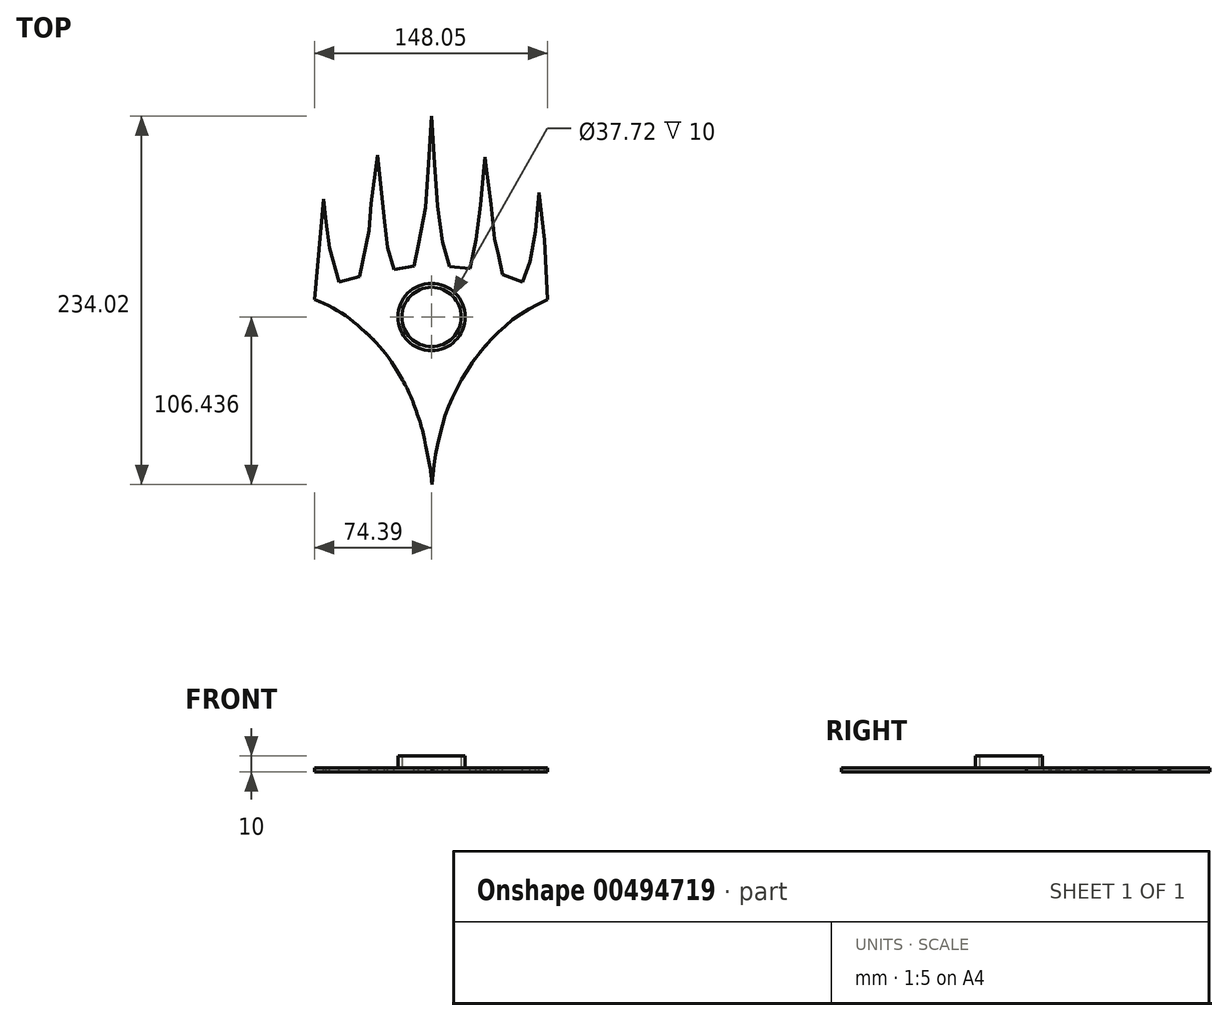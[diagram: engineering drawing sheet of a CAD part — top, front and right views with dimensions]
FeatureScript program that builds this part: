
annotation { "Feature Type Name" : "Feature", "Feature Type Description" : "" }
export const myFeature = defineFeature(function(context is Context, id is Id, definition is map)
    precondition{}
    {
        {
            var Q0;
            Q0=qCreatedBy(makeId("Top.planeOp"),FACE);
            var sketch = newSketch(context, id + "F0", { "sketchPlane" : qUnion([Q0])});
            skFitSpline(sketch, "E0", {"points": [v(-77.05, -65.7) * mm, v(-66.03, -70.4) * mm, v(-54.89, -77.21) * mm, v(-43.29, -86.88) * mm, v(-32.6, -98.12) * mm, v(-24.04, -110.73) * mm, v(-17.04, -122.98) * mm, v(-12.72, -133.75) * mm, v(-8.2, -147.47) * mm, v(-6, -157.78) * mm, v(-3.7, -169.2) * mm, v(-2.04, -183.84) * mm, v(0, -199.35) * mm, v(2.57, -183.84) * mm, v(4.13, -169.11) * mm, v(8.46, -147.75) * mm, v(12.79, -134.03) * mm, v(18.87, -120.86) * mm, v(25.86, -108.52) * mm, v(32.3, -99.6) * mm, v(45.94, -84.95) * mm, v(59.01, -74.73) * mm, v(76.23, -65.43) * mm], "startDerivative": vector(270.48, -105.81) * mm, "endDerivative": vector(345.36, 173.77) * mm});
            skLineSegment(sketch, "E1", {"start": v(-77.05, -65.7) * mm, "end": v(-69.5, 18.42) * mm});
            skLineSegment(sketch, "E2", {"start": v(-69.5, 18.42) * mm, "end": v(-69.69, 16.3) * mm});
            skLineSegment(sketch, "E3", {"start": v(-68.1, 15.93) * mm, "end": v(-64.46, -14.58) * mm});
            skLineSegment(sketch, "E4", {"start": v(-64.46, -14.58) * mm, "end": v(-62.19, -30.96) * mm});
            skLineSegment(sketch, "E5", {"start": v(-62.19, -30.96) * mm, "end": v(-56.9, -49.85) * mm});
            skLineSegment(sketch, "E6", {"start": v(-56.9, -49.85) * mm, "end": v(-47.8, -47.3) * mm});
            skLineSegment(sketch, "E7", {"start": v(-47.8, -47.3) * mm, "end": v(-42.29, -19.87) * mm});
            skLineSegment(sketch, "E8", {"start": v(-42.29, -19.87) * mm, "end": v(-40.76, -2.9) * mm});
            skLineSegment(sketch, "E9", {"start": v(-40.76, -2.9) * mm, "end": v(-34.22, 49.4) * mm});
            skLineSegment(sketch, "E10", {"start": v(-34.22, 49.4) * mm, "end": v(-27.42, -14.33) * mm});
            skLineSegment(sketch, "E11", {"start": v(-27.42, -14.33) * mm, "end": v(-25.4, -30.45) * mm});
            skLineSegment(sketch, "E12", {"start": v(-25.4, -30.45) * mm, "end": v(-22.13, -42.04) * mm});
            skLineSegment(sketch, "E13", {"start": v(-22.13, -42.04) * mm, "end": v(-13.06, -40.53) * mm});
            skLineSegment(sketch, "E14", {"start": v(-13.06, -40.53) * mm, "end": v(-10.54, -28.19) * mm});
            skLineSegment(sketch, "E15", {"start": v(-10.54, -28.19) * mm, "end": v(-6.26, -5.26) * mm});
            skLineSegment(sketch, "E16", {"start": v(-6.26, -5.26) * mm, "end": v(-4.5, 22.45) * mm});
            skLineSegment(sketch, "E17", {"start": v(-4.5, 22.45) * mm, "end": v(-0.97, 76.11) * mm});
            skLineSegment(sketch, "E18", {"start": v(-0.97, 76.11) * mm, "end": v(1.05, 76.11) * mm});
            skLineSegment(sketch, "E19", {"start": v(1.05, 76.11) * mm, "end": v(4.32, 22.45) * mm});
            skLineSegment(sketch, "E20", {"start": v(4.32, 22.45) * mm, "end": v(6.34, -4.5) * mm});
            skLineSegment(sketch, "E21", {"start": v(6.34, -4.5) * mm, "end": v(9.36, -26.93) * mm});
            skLineSegment(sketch, "E22", {"start": v(9.36, -26.93) * mm, "end": v(13.4, -40.78) * mm});
            skLineSegment(sketch, "E23", {"start": v(13.4, -40.78) * mm, "end": v(22.46, -41.54) * mm});
            skLineSegment(sketch, "E24", {"start": v(22.46, -41.54) * mm, "end": v(25.74, -25.42) * mm});
            skLineSegment(sketch, "E25", {"start": v(25.74, -25.42) * mm, "end": v(28.5, -3.75) * mm});
            skLineSegment(sketch, "E26", {"start": v(28.5, -3.75) * mm, "end": v(30.77, 20.69) * mm});
            skLineSegment(sketch, "E27", {"start": v(30.77, 20.69) * mm, "end": v(34.3, 48.9) * mm});
            skLineSegment(sketch, "E28", {"start": v(34.3, 48.9) * mm, "end": v(37.07, 20.94) * mm});
            skLineSegment(sketch, "E29", {"start": v(37.07, 20.94) * mm, "end": v(40.35, -3) * mm});
            skLineSegment(sketch, "E30", {"start": v(40.35, -3) * mm, "end": v(42.61, -25.16) * mm});
            skLineSegment(sketch, "E31", {"start": v(42.61, -25.16) * mm, "end": v(45.13, -35.24) * mm});
            skLineSegment(sketch, "E32", {"start": v(45.13, -35.24) * mm, "end": v(47.4, -46.33) * mm});
            skLineSegment(sketch, "E33", {"start": v(47.4, -46.33) * mm, "end": v(56.22, -49.6) * mm});
            skLineSegment(sketch, "E34", {"start": v(56.22, -49.6) * mm, "end": v(60.25, -39.27) * mm});
            skLineSegment(sketch, "E35", {"start": v(60.25, -39.27) * mm, "end": v(63.52, -20.12) * mm});
            skLineSegment(sketch, "E36", {"start": v(63.52, -20.12) * mm, "end": v(66.3, 7.84) * mm});
            skLineSegment(sketch, "E37", {"start": v(66.3, 7.84) * mm, "end": v(68.82, 18.17) * mm});
            skLineSegment(sketch, "E38", {"start": v(68.82, 18.17) * mm, "end": v(69.57, 15.9) * mm});
            skLineSegment(sketch, "E39", {"start": v(69.57, 15.9) * mm, "end": v(74.36, -26.17) * mm});
            skLineSegment(sketch, "E40", {"start": v(74.36, -26.17) * mm, "end": v(76.23, -65.43) * mm});
            skLineSegment(sketch, "E41", {"start": v(-68.1, 15.93) * mm, "end": v(-69.5, 18.42) * mm});
            skCircle(sketch, "E42", {"center": v(0, -75.1) * mm, "radius": 18.86 * mm});
            skSolve(sketch);
        }
        {
            var Q0;
            Q0 = qSketchRegion(id + "F0", true);
            extrude(context, id + "F1", {"entities" : qUnion([Q0]), "depth" : 10 * mm});
        }
        {
            var Q0;
            Q0=makeQuery(id+"F1.opExtrude","CAP_FACE",FACE,{"disambiguationData":[OSD([sQuery(id+"F0.wireOp",EDGE,"E0"),sQuery(id+"F0.wireOp",EDGE,"E1"),sQuery(id+"F0.wireOp",EDGE,"E2"),sQuery(id+"F0.wireOp",EDGE,"E3"),sQuery(id+"F0.wireOp",EDGE,"E4"),sQuery(id+"F0.wireOp",EDGE,"E5"),sQuery(id+"F0.wireOp",EDGE,"E6"),sQuery(id+"F0.wireOp",EDGE,"E7"),sQuery(id+"F0.wireOp",EDGE,"E8"),sQuery(id+"F0.wireOp",EDGE,"E9"),sQuery(id+"F0.wireOp",EDGE,"E10"),sQuery(id+"F0.wireOp",EDGE,"E11"),sQuery(id+"F0.wireOp",EDGE,"E12"),sQuery(id+"F0.wireOp",EDGE,"E13"),sQuery(id+"F0.wireOp",EDGE,"E14"),sQuery(id+"F0.wireOp",EDGE,"E15"),sQuery(id+"F0.wireOp",EDGE,"E16"),sQuery(id+"F0.wireOp",EDGE,"E17"),sQuery(id+"F0.wireOp",EDGE,"E18"),sQuery(id+"F0.wireOp",EDGE,"E19"),sQuery(id+"F0.wireOp",EDGE,"E20"),sQuery(id+"F0.wireOp",EDGE,"E21"),sQuery(id+"F0.wireOp",EDGE,"E22"),sQuery(id+"F0.wireOp",EDGE,"E23"),sQuery(id+"F0.wireOp",EDGE,"E24"),sQuery(id+"F0.wireOp",EDGE,"E25"),sQuery(id+"F0.wireOp",EDGE,"E26"),sQuery(id+"F0.wireOp",EDGE,"E27"),sQuery(id+"F0.wireOp",EDGE,"E28"),sQuery(id+"F0.wireOp",EDGE,"E29"),sQuery(id+"F0.wireOp",EDGE,"E30"),sQuery(id+"F0.wireOp",EDGE,"E31"),sQuery(id+"F0.wireOp",EDGE,"E32"),sQuery(id+"F0.wireOp",EDGE,"E33"),sQuery(id+"F0.wireOp",EDGE,"E34"),sQuery(id+"F0.wireOp",EDGE,"E35"),sQuery(id+"F0.wireOp",EDGE,"E36"),sQuery(id+"F0.wireOp",EDGE,"E37"),sQuery(id+"F0.wireOp",EDGE,"E38"),sQuery(id+"F0.wireOp",EDGE,"E39"),sQuery(id+"F0.wireOp",EDGE,"E40"),sQuery(id+"F0.wireOp",EDGE,"E41")])],"isStart":false});
            shell(context, id + "F2", {"entities" : qUnion([Q0]), "thickness" : 2.5 * mm});
        }
        {
            var Q0;
            {var subQ0=sQuery(id+"F0.wireOp",EDGE,"E42");var subQ1=sQuery(id+"F0.wireOp",EDGE,"E41");var subQ2=sQuery(id+"F0.wireOp",EDGE,"E40");var subQ3=sQuery(id+"F0.wireOp",EDGE,"E39");var subQ4=sQuery(id+"F0.wireOp",EDGE,"E38");var subQ5=sQuery(id+"F0.wireOp",EDGE,"E37");var subQ6=sQuery(id+"F0.wireOp",EDGE,"E36");var subQ7=sQuery(id+"F0.wireOp",EDGE,"E35");var subQ8=sQuery(id+"F0.wireOp",EDGE,"E34");var subQ9=sQuery(id+"F0.wireOp",EDGE,"E33");var subQ10=sQuery(id+"F0.wireOp",EDGE,"E32");var subQ11=sQuery(id+"F0.wireOp",EDGE,"E31");var subQ12=sQuery(id+"F0.wireOp",EDGE,"E30");var subQ13=sQuery(id+"F0.wireOp",EDGE,"E29");var subQ14=sQuery(id+"F0.wireOp",EDGE,"E28");var subQ15=sQuery(id+"F0.wireOp",EDGE,"E27");var subQ16=sQuery(id+"F0.wireOp",EDGE,"E26");var subQ17=sQuery(id+"F0.wireOp",EDGE,"E25");var subQ18=sQuery(id+"F0.wireOp",EDGE,"E24");var subQ19=sQuery(id+"F0.wireOp",EDGE,"E23");var subQ20=sQuery(id+"F0.wireOp",EDGE,"E22");var subQ21=sQuery(id+"F0.wireOp",EDGE,"E21");var subQ22=sQuery(id+"F0.wireOp",EDGE,"E20");var subQ23=sQuery(id+"F0.wireOp",EDGE,"E19");var subQ24=sQuery(id+"F0.wireOp",EDGE,"E18");var subQ25=sQuery(id+"F0.wireOp",EDGE,"E17");var subQ26=sQuery(id+"F0.wireOp",EDGE,"E16");var subQ27=sQuery(id+"F0.wireOp",EDGE,"E15");var subQ28=sQuery(id+"F0.wireOp",EDGE,"E14");var subQ29=sQuery(id+"F0.wireOp",EDGE,"E13");var subQ30=sQuery(id+"F0.wireOp",EDGE,"E12");var subQ31=sQuery(id+"F0.wireOp",EDGE,"E11");var subQ32=sQuery(id+"F0.wireOp",EDGE,"E10");var subQ33=sQuery(id+"F0.wireOp",EDGE,"E9");var subQ34=sQuery(id+"F0.wireOp",EDGE,"E8");var subQ35=sQuery(id+"F0.wireOp",EDGE,"E7");var subQ36=sQuery(id+"F0.wireOp",EDGE,"E6");var subQ37=sQuery(id+"F0.wireOp",EDGE,"E5");var subQ38=sQuery(id+"F0.wireOp",EDGE,"E4");var subQ39=sQuery(id+"F0.wireOp",EDGE,"E3");var subQ40=sQuery(id+"F0.wireOp",EDGE,"E2");var subQ41=sQuery(id+"F0.wireOp",EDGE,"E1");var subQ42=sQuery(id+"F0.wireOp",EDGE,"E0");Q0=makeQuery(id+"F2.opShell","OFFSET_FACE",FACE,{"disambiguationData":[OSD([subQ42,subQ41,subQ40,subQ39,subQ38,subQ37,subQ36,subQ35,subQ34,subQ33,subQ32,subQ31,subQ30,subQ29,subQ28,subQ27,subQ26,subQ25,subQ24,subQ23,subQ22,subQ21,subQ20,subQ19,subQ18,subQ17,subQ16,subQ15,subQ14,subQ13,subQ12,subQ11,subQ10,subQ9,subQ8,subQ7,subQ6,subQ5,subQ4,subQ3,subQ2,subQ1,subQ0]),TDD([makeQuery(id+"F1.opExtrude","CAP_FACE",FACE,{"disambiguationData":[OSD([subQ42,subQ41,subQ40,subQ39,subQ38,subQ37,subQ36,subQ35,subQ34,subQ33,subQ32,subQ31,subQ30,subQ29,subQ28,subQ27,subQ26,subQ25,subQ24,subQ23,subQ22,subQ21,subQ20,subQ19,subQ18,subQ17,subQ16,subQ15,subQ14,subQ13,subQ12,subQ11,subQ10,subQ9,subQ8,subQ7,subQ6,subQ5,subQ4,subQ3,subQ2,subQ1,subQ0])],"isStart":false})])]});}
            extrude(context, id + "F3", {"entities" : qUnion([Q0]), "operationType" : NewBodyOperationType.REMOVE, "oppositeDirection" : true, "depth" : 115 * mm});
        }
    });
